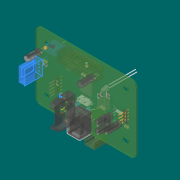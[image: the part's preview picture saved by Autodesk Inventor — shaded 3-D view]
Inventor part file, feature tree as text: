
AUTODESK INVENTOR PART (.ipt)
format: ipt  version: 2019 (Build 230136000, 136)  size: 22,323,200 bytes
history: native  units: mm
features: sketch x26, other x3
ambient origin geometry x8: Origin, YZ Plane, XZ Plane, XY Plane, X Axis, Y Axis, Z Axis, Center Point
bodies: Body1 (feature_tree), Body2 (feature_tree), Body3 (feature_tree), Body4 (feature_tree), Body5 (feature_tree), Body6 (feature_tree), Body7 (feature_tree), Body8 (feature_tree), Body9 (feature_tree), Body10 (feature_tree), Body11 (feature_tree), Body12 (feature_tree), Body13 (feature_tree), Body14 (feature_tree), Body15 (feature_tree), Body16 (feature_tree), Body17 (feature_tree), Body18 (feature_tree), Body19 (feature_tree), Body20 (feature_tree), Body21 (feature_tree), Body22 (feature_tree), Body23 (feature_tree), Body24 (feature_tree), Body25 (feature_tree), Body26 (feature_tree), Body27 (feature_tree), Body28 (feature_tree), Body29 (feature_tree), Body30 (feature_tree), Body31 (feature_tree), Body32 (feature_tree), Body33 (feature_tree), Body34 (feature_tree), Body35 (feature_tree), Body36 (feature_tree), Body37 (feature_tree), Body38 (feature_tree), Body39 (feature_tree), Body40 (feature_tree), Body41 (feature_tree), Body42 (feature_tree), Body43 (feature_tree), Body44 (feature_tree), Body45 (feature_tree), Body46 (feature_tree), Body47 (feature_tree), Body48 (feature_tree), Body49 (feature_tree), Body50 (feature_tree), Body51 (feature_tree), Body52 (feature_tree), Body53 (feature_tree), Body54 (feature_tree), Body55 (feature_tree), Body56 (feature_tree), Body57 (feature_tree), Body58 (feature_tree), Body59 (feature_tree), Body60 (feature_tree), Body61 (feature_tree), Body62 (feature_tree), Body63 (feature_tree), Body64 (feature_tree), Body65 (feature_tree), Body66 (feature_tree), Body67 (feature_tree), Body68 (feature_tree), Body69 (feature_tree), Body70 (feature_tree), Body71 (feature_tree), Body72 (feature_tree), Body73 (feature_tree), Body74 (feature_tree), Body75 (feature_tree), Body76 (feature_tree), Body77 (feature_tree), Body78 (feature_tree), Body79 (feature_tree), Body80 (feature_tree), Body81 (feature_tree), Body82 (feature_tree), Body83 (feature_tree), Body84 (feature_tree), Body85 (feature_tree), Body86 (feature_tree), Body87 (feature_tree), Body88 (feature_tree), Body89 (feature_tree), Body90 (feature_tree), Body91 (feature_tree), Body92 (feature_tree), Body93 (feature_tree), Body94 (feature_tree), Body95 (feature_tree), Body96 (feature_tree), Body97 (feature_tree), Body98 (feature_tree), Body99 (feature_tree), Body100 (feature_tree), Body101 (feature_tree), Body102 (feature_tree), Body103 (feature_tree), Body104 (feature_tree), Body105 (feature_tree), Body106 (feature_tree), Body107 (feature_tree), Body108 (feature_tree), Body109 (feature_tree), Body110 (feature_tree), Body111 (feature_tree), Body112 (feature_tree), Body113 (feature_tree), Body114 (feature_tree), Body115 (feature_tree), Body116 (feature_tree), Body117 (feature_tree), Body118 (feature_tree), Body119 (feature_tree), Body120 (feature_tree), Body121 (feature_tree), Body122 (feature_tree), Body123 (feature_tree), Body124 (feature_tree), Body125 (feature_tree), Body126 (feature_tree), Body127 (feature_tree), Body128 (feature_tree), Body129 (feature_tree), Body130 (feature_tree), Body131 (feature_tree), Body132 (feature_tree), Body133 (feature_tree), Body134 (feature_tree), Body135 (feature_tree), Body136 (feature_tree), Body137 (feature_tree), Body138 (feature_tree), Body139 (feature_tree), Body140 (feature_tree), Body141 (feature_tree), Body142 (feature_tree), Body143 (feature_tree), Body144 (feature_tree), Body145 (feature_tree), Body146 (feature_tree), Body147 (feature_tree), Body148 (feature_tree), Body149 (feature_tree), Body150 (feature_tree), Body151 (feature_tree), Body152 (feature_tree), Body153 (feature_tree), Body154 (feature_tree), Body155 (feature_tree), Body156 (feature_tree), Body157 (feature_tree), Body158 (feature_tree), Body159 (feature_tree), Body160 (feature_tree), Body161 (feature_tree), Body162 (feature_tree), Body163 (feature_tree), Body164 (feature_tree), Body165 (feature_tree), Body166 (feature_tree), Body167 (feature_tree), Body168 (feature_tree), Body169 (feature_tree), Body170 (feature_tree), Body171 (feature_tree), Body172 (feature_tree), Body173 (feature_tree), Body174 (feature_tree), Body175 (feature_tree), Body176 (feature_tree), Body177 (feature_tree), Body178 (feature_tree), Body179 (feature_tree), Body180 (feature_tree), Body181 (feature_tree), Body182 (feature_tree), Body183 (feature_tree), Body184 (feature_tree), Body185 (feature_tree), Body186 (feature_tree), Body187 (feature_tree), Body188 (feature_tree), Body189 (feature_tree), Body190 (feature_tree), Body191 (feature_tree), Body192 (feature_tree), Body193 (feature_tree), Body194 (feature_tree), Body195 (feature_tree), Body196 (feature_tree), Body197 (feature_tree), Body198 (feature_tree), Body199 (feature_tree), Body200 (feature_tree), Body201 (feature_tree), Body202 (feature_tree), Body203 (feature_tree), Body204 (feature_tree), Body205 (feature_tree), Body206 (feature_tree), Body207 (feature_tree), Body208 (feature_tree), Body209 (feature_tree), Body210 (feature_tree), Body211 (feature_tree), Body212 (feature_tree), Body213 (feature_tree), Body214 (feature_tree), Body215 (feature_tree), Body216 (feature_tree), Body217 (feature_tree), Body218 (feature_tree), Body219 (feature_tree), Body220 (feature_tree), Body221 (feature_tree), Body222 (feature_tree), Body223 (feature_tree), Body224 (feature_tree), Body225 (feature_tree), Body226 (feature_tree), Body227 (feature_tree), Body228 (feature_tree), Body229 (feature_tree), Body230 (feature_tree), Body231 (feature_tree), Body232 (feature_tree), Body233 (feature_tree), Body234 (feature_tree), Body235 (feature_tree), Body236 (feature_tree), Body237 (feature_tree), Body238 (feature_tree), Body239 (feature_tree), Body240 (feature_tree), Body241 (feature_tree), Body242 (feature_tree), Body243 (feature_tree), Body244 (feature_tree), Body245 (feature_tree), Body246 (feature_tree), Body247 (feature_tree), Body248 (feature_tree), Body249 (feature_tree), Body250 (feature_tree), Body251 (feature_tree), Body252 (feature_tree), Body253 (feature_tree), Body254 (feature_tree), Body255 (feature_tree), Body256 (feature_tree), Body257 (feature_tree), Body258 (feature_tree), Body259 (feature_tree), Body260 (feature_tree), Body261 (feature_tree), Body262 (feature_tree), Body263 (feature_tree), Body264 (feature_tree), Body265 (feature_tree), Body266 (feature_tree), Body267 (feature_tree), Body268 (feature_tree), Body269 (feature_tree), Body270 (feature_tree), Body271 (feature_tree), Body272 (feature_tree), Body273 (feature_tree), Body274 (feature_tree), Body275 (feature_tree), Body276 (feature_tree), Body277 (feature_tree), Body278 (feature_tree), Body279 (feature_tree), Body280 (feature_tree), Body281 (feature_tree), Body282 (feature_tree), Body283 (feature_tree), Body284 (feature_tree), Body285 (feature_tree), Body286 (feature_tree), Body287 (feature_tree), Body288 (feature_tree), Body289 (feature_tree), Body290 (feature_tree), Body291 (feature_tree), Body292 (feature_tree), Body293 (feature_tree), Body294 (feature_tree), Body295 (feature_tree), Body296 (feature_tree), Body297 (feature_tree), Body298 (feature_tree), Body299 (feature_tree), Body300 (feature_tree), Body301 (feature_tree), Body302 (feature_tree), Body303 (feature_tree), Body304 (feature_tree), Body305 (feature_tree), Body306 (feature_tree), Body307 (feature_tree), Body308 (feature_tree), Body309 (feature_tree), Body310 (feature_tree), Body311 (feature_tree), Body312 (feature_tree), Body313 (feature_tree), Body314 (feature_tree), Body315 (feature_tree), Body316 (feature_tree), Body317 (feature_tree), Body318 (feature_tree), Body319 (feature_tree), Body320 (feature_tree), Body321 (feature_tree), Body322 (feature_tree), Body323 (feature_tree), Body324 (feature_tree), Body325 (feature_tree), Body326 (feature_tree), Body327 (feature_tree), Body328 (feature_tree), Body329 (feature_tree), Body330 (feature_tree), Body331 (feature_tree), Body332 (feature_tree), Body333 (feature_tree), Body334 (feature_tree), Body335 (feature_tree), Body336 (feature_tree), Body337 (feature_tree), Body338 (feature_tree), Body339 (feature_tree), Body340 (feature_tree), Body341 (feature_tree), Body342 (feature_tree), Body343 (feature_tree), Body344 (feature_tree), Body345 (feature_tree), Body346 (feature_tree), Body347 (feature_tree), Body348 (feature_tree), Body349 (feature_tree), Body350 (feature_tree), Body351 (feature_tree), Body352 (feature_tree), Body353 (feature_tree), Body354 (feature_tree), Body355 (feature_tree), Body356 (feature_tree), Body357 (feature_tree), Body358 (feature_tree), Body359 (feature_tree), Body360 (feature_tree), Body361 (feature_tree), Body362 (feature_tree), Body363 (feature_tree), Body364 (feature_tree), Body365 (feature_tree), Body366 (feature_tree), Body367 (feature_tree), Body368 (feature_tree), Body369 (feature_tree), Body370 (feature_tree), Body371 (feature_tree), Body372 (feature_tree), Body373 (feature_tree), Body374 (feature_tree), Body375 (feature_tree), Body376 (feature_tree), Body377 (feature_tree), Body378 (feature_tree), Body379 (feature_tree), Body380 (feature_tree), Body381 (feature_tree), Body382 (feature_tree), Body383 (feature_tree), Body384 (feature_tree), Body385 (feature_tree), Body386 (feature_tree), Body387 (feature_tree), Body388 (feature_tree), Body389 (feature_tree), Body390 (feature_tree), Body391 (feature_tree), Body392 (feature_tree), Body393 (feature_tree), Body394 (feature_tree), Body395 (feature_tree), Body396 (feature_tree), Body397 (feature_tree), Body398 (feature_tree), Body399 (feature_tree), Body400 (feature_tree), Body401 (feature_tree), Body402 (feature_tree)
feature tree (29):
  other  "Repaired Geometry1"
  sketch  "3D Sketch1"
  sketch  "3D Sketch2"
  sketch  "3D Sketch3"
  sketch  "3D Sketch4"
  sketch  "3D Sketch5"
  sketch  "3D Sketch6"
  sketch  "3D Sketch7"
  sketch  "3D Sketch8"
  sketch  "3D Sketch9"
  sketch  "3D Sketch10"
  sketch  "3D Sketch11"
  sketch  "3D Sketch12"
  sketch  "3D Sketch13"
  sketch  "3D Sketch14"
  sketch  "3D Sketch15"
  sketch  "3D Sketch16"
  sketch  "3D Sketch17"
  sketch  "3D Sketch18"
  sketch  "3D Sketch19"
  sketch  "3D Sketch20"
  sketch  "3D Sketch21"
  sketch  "3D Sketch22"
  sketch  "3D Sketch23"
  sketch  "3D Sketch24"
  sketch  "Sketch1"
  sketch  "3D Sketch25"
  other  "Composite1"
  other  "Srf1"
